# Revit family: 0053892
name_source: partatom
category: Lighting Fixtures
revit_build: Autodesk Revit 2016 (Build: 20150220_1215(x64)
units: mm (PartAtom-declared; Revit-internal decimal feet)

## family parameters
Cut with Voids When Loaded = No
Host = Face
Light Source = Yes
OmniClass Number = 23.80.70.11.14.11
OmniClass Title = Downlights
Part Type = Normal
Room Calculation Point = No
Round Connector Dimension = Use Diameter
Shared = No

## types (1)
- 0053892 ST eco Downlight Flat 205 IP44 1750lm 830 DIM
    AccessoryMaterial = Diffuser-Sylvania-Glow
    Apparent Load = 18 VA
    Assembly Code = D5020200
    AssetType = Fixed
    BodyHeight_FEILO = 13 mm
    BodyLength_FEILO = 222 mm
    BodyMaterial = Body-Sylvania-SylFlatDimmable-White
    BodyWidth_FEILO = 222 mm
    ClassificationName = Uniclass2015
    ClassificationValue = EF_70_80
    Color Filter = 16777215
    Cost = 0 $
    CutoutHeight_FEILO = 36 mm
    Default Elevation = 1219 mm
    Description = Integrated LED recessed downlight providing 1620 fixture lumens at a wattage of 18W giving a high efficacy of 90lm/W. Fitting includes Leading/Trailing edge phase dimmable driver and has a round ceiling cut out of 205mm with an IP20 and IK02 rating providing uniform distribution with an Opal diffuser and 110° beam angle. Provided including a Loop in Loop out box and built Built white aluminium housing.
    DiffuserMaterial = Diffuser-Sylvania-Glow
    Dimming Lamp Color Temperature Shift = <None>
    DimmingControlOptions = Dimmable
    DocumentationLiterature = http://www.sylvania-lighting.com
    DurationUnit = hours
    ElectricShockClassification = Class II
    Emit Shape Visible in Rendering = No
    Emit from Circle Diameter = 182 mm  [stored 0.597113 ft]
    ExpectedLife = 50000
    IfcExportAs = IfcLightFixtureType
    IfcExportType = IfcLightFixtureType
    ImpactProtectionIndex = IK06
    IngressProtection = IP44
    InputNominalFrequency = 50/60 Hz
    InputVoltage = 220-240V~
    Keynote = 16500
    Lamp = LED
    LampColourRenderingIndex = 80
    LampColourTemperature = 3000 K
    LampNominalLuminous = 1750 lm
    LampsType = LED
    LightOutputRatio = 1
    LuminaireType = LED recessed downlight
    LuminousEfficacy = 97.22 lm/W
    Manufacturer = Feilo Sylvania
    ManufacturerName = Feilo Sylvania
    Material = Aluminium
    Model = ST eco Downlight Flat 205 IP44 1750lm 830 DIM
    ModelNumber = 0053892
    ModelReference = ST eco Downlight Flat 205 IP44 1750lm 830 DIM
    Name = ST eco Downlight Flat 205 IP44 1750lm 830 DIM
    NominalDepth = 222 mm
    NominalHeight = 26 mm
    NominalLength = 222 mm
    Photometric Web File = 0053892.ies
    PowerConsumption = 18 W
    PowerFactor = 0
    RecessedDiameter_FEILO = 205 mm  [stored 0.672572 ft]
    RecessedHeight_FEILO = 26 mm
    ReflectorMaterial = <By Category>
    SpringMountEndAngle_FEILO = 10.00°
    SpringMountStartAngle_FEILO = -10.00°
    Tilt Angle = -90.00°
    Type Image = <None>
    TypeName = ST eco Downlight Flat 205 IP44 1750lm 830 DIM
    URL = http://www.sylvania-lighting.com
    Voltage = 230 V
    WarrantyDurationUnit = year
    Weight = 6.54 kg

note: [stored X ft] marks values corroborated as IEEE doubles in the binary element streams (Revit-internal decimal feet)

## geometry (parser evidence)
native form markers: Sweep x2
no freeform markers — native parametric forms only
